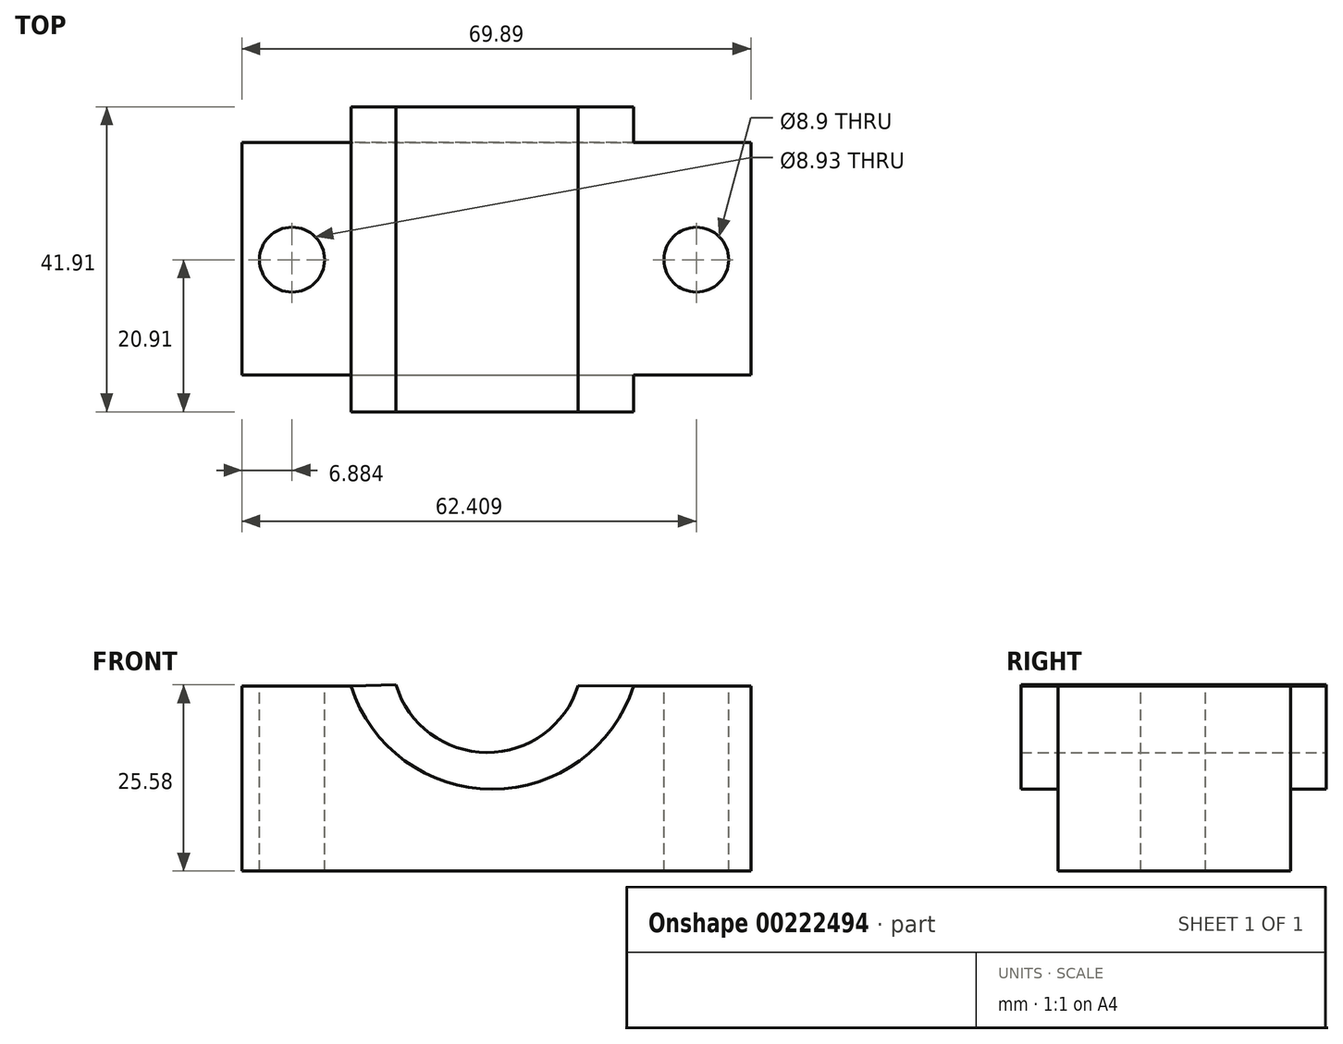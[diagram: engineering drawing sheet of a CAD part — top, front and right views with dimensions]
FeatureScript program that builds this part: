
annotation { "Feature Type Name" : "Feature", "Feature Type Description" : "" }
export const myFeature = defineFeature(function(context is Context, id is Id, definition is map)
    precondition{}
    {
        {
            var Q0;
            Q0=qCreatedBy(makeId("Top.planeOp"),FACE);
            var sketch = newSketch(context, id + "F0", { "sketchPlane" : qUnion([Q0])});
            skLineSegment(sketch, "E0.bottom", {"start": v(-32.95, 16.12) * mm, "end": v(36.94, 16.12) * mm});
            skLineSegment(sketch, "E0.top", {"start": v(-32.95, -15.83) * mm, "end": v(36.94, -15.83) * mm});
            skLineSegment(sketch, "E0.left", {"start": v(-32.95, 16.12) * mm, "end": v(-32.95, -15.83) * mm});
            skLineSegment(sketch, "E0.right", {"start": v(36.94, 16.12) * mm, "end": v(36.94, -15.83) * mm});
            skSolve(sketch);
        }
        {
            var Q0;
            Q0 = qSketchRegion(id + "F0", true);
            extrude(context, id + "F1", {"entities" : qUnion([Q0]), "depth" : 25.4 * mm});
        }
        {
            var Q0;
            Q0=makeQuery(id+"F1.opExtrude","SWEPT_FACE",FACE,{"disambiguationData":[OSD([sQuery(id+"F0.wireOp",EDGE,"E0.top")])]});
            var sketch = newSketch(context, id + "F2", { "sketchPlane" : qUnion([Q0])});
            skArc(sketch, "E1", {"start": v(-17.97, 25.4) * mm, "mid": v(1.43, 11.24) * mm, "end": v(20.82, 25.4) * mm});
            skLineSegment(sketch, "E2", {"start": v(-17.97, 25.4) * mm, "end": v(20.82, 25.4) * mm});
            skSolve(sketch);
        }
        {
            var Q0;
            Q0=makeQuery(id+"F2.imprint","IMPRINT",FACE,{"disambiguationData":[TD([[makeQuery(id+"F2.imprint","IMPRINT",EDGE,{"derivedFrom":sQuery(id+"F2.wireOp",EDGE,"E1")}),1.0]])]});
            extrude(context, id + "F3", {"entities" : qUnion([Q0]), "operationType" : NewBodyOperationType.REMOVE, "endBound" : BoundingType.THROUGH_ALL, "oppositeDirection" : true, "depth" : 25.4 * mm});
        }
        {
            var Q0;
            Q0=makeQuery(id+"F1.opExtrude","SWEPT_FACE",FACE,{"disambiguationData":[OSD([sQuery(id+"F0.wireOp",EDGE,"E0.top")])]});
            var sketch = newSketch(context, id + "F4", { "sketchPlane" : qUnion([Q0])});
            skArc(sketch, "E3", {"start": v(-11.8, 25.58) * mm, "mid": v(0.67, 16.3) * mm, "end": v(13.23, 25.45) * mm});
            skLineSegment(sketch, "E4", {"start": v(-17.97, 25.4) * mm, "end": v(-11.8, 25.58) * mm});
            skLineSegment(sketch, "E5", {"start": v(13.23, 25.45) * mm, "end": v(20.82, 25.4) * mm});
            skSolve(sketch);
        }
        {
            var Q0;
            Q0=makeQuery(id+"F4.imprint","IMPRINT",FACE,{"disambiguationData":[TD([[makeQuery(id+"F4.imprint","IMPRINT",EDGE,{"derivedFrom":sQuery(id+"F4.wireOp",EDGE,"E3")}),-1.0]])]});
            extrude(context, id + "F5", {"entities" : qUnion([Q0]), "operationType" : NewBodyOperationType.ADD, "depth" : 5.08 * mm, "hasSecondDirection" : true, "secondDirectionOppositeDirection" : true, "secondDirectionDepth" : 36.83 * mm});
        }
        {
            var Q0;
            {var subQ0=sQuery(id+"F0.wireOp",EDGE,"E0.bottom");var subQ1=sQuery(id+"F0.wireOp",EDGE,"E0.top");var subQ2=sQuery(id+"F0.wireOp",EDGE,"E0.right");Q0=makeQuery(id+"F3.boolean.opBoolean","SPLIT",FACE,{"disambiguationData":[TD([makeQuery(id+"F1.opExtrude","SWEPT_FACE",FACE,{"disambiguationData":[OSD([subQ2])]})])],"derivedFrom":makeQuery(id+"F1.opExtrude","CAP_FACE",FACE,{"disambiguationData":[OSD([subQ0,subQ1,sQuery(id+"F0.wireOp",EDGE,"E0.left"),subQ2])],"isStart":false})});}
            var sketch = newSketch(context, id + "F6", { "sketchPlane" : qUnion([Q0])});
            skCircle(sketch, "E6", {"center": v(-26.07, 0) * mm, "radius": 4.47 * mm});
            skCircle(sketch, "E7", {"center": v(29.46, 0) * mm, "radius": 4.45 * mm});
            skSolve(sketch);
        }
        {
            var Q0;
            Q0 = qSketchRegion(id + "F6", true);
            extrude(context, id + "F7", {"entities" : qUnion([Q0]), "operationType" : NewBodyOperationType.REMOVE, "endBound" : BoundingType.THROUGH_ALL, "oppositeDirection" : true, "depth" : 25.4 * mm});
        }
    });
